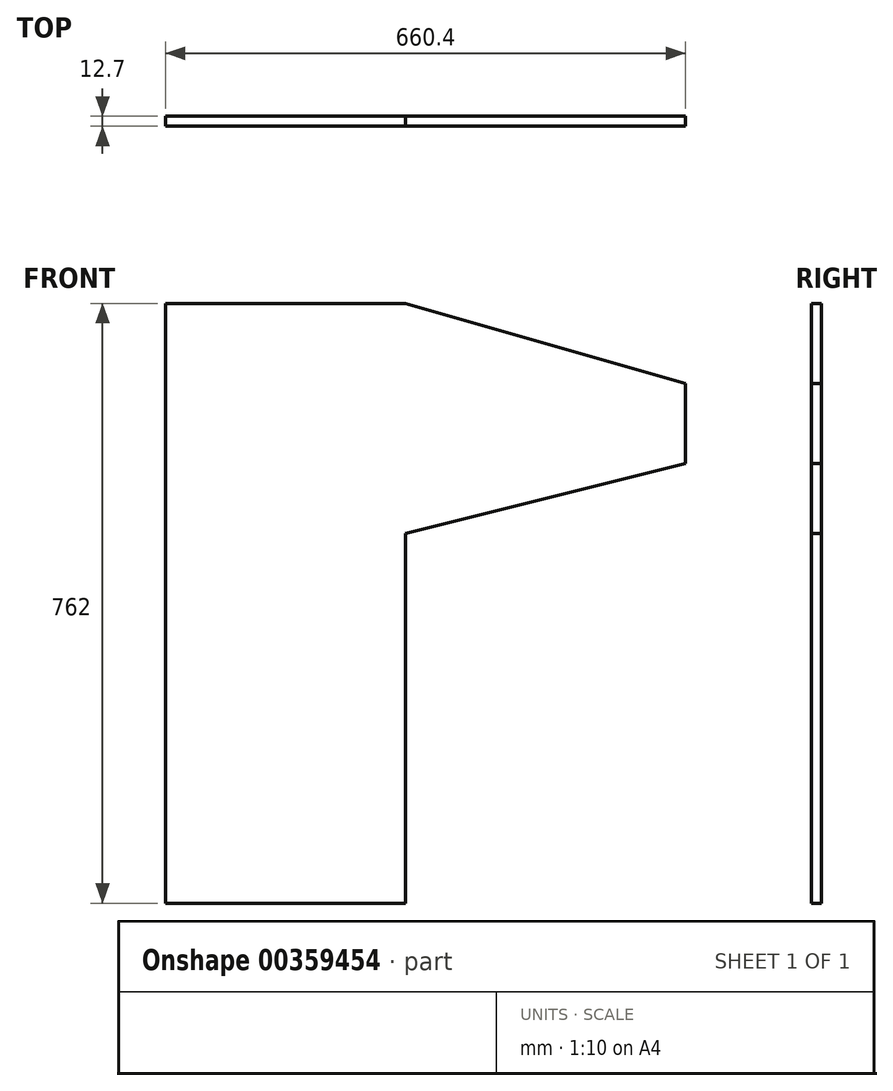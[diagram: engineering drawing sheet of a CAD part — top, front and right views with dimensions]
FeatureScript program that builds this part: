
annotation { "Feature Type Name" : "Feature", "Feature Type Description" : "" }
export const myFeature = defineFeature(function(context is Context, id is Id, definition is map)
    precondition{}
    {
        {
            var Q0;
            Q0=qCreatedBy(makeId("Front.planeOp"),FACE);
            var sketch = newSketch(context, id + "F0", { "sketchPlane" : qUnion([Q0])});
            skLineSegment(sketch, "E0", {"start": v(0, 0) * mm, "end": v(0, 762) * mm});
            skLineSegment(sketch, "E1", {"start": v(0, 762) * mm, "end": v(304.8, 762) * mm});
            skLineSegment(sketch, "E2", {"start": v(304.8, 762) * mm, "end": v(660.4, 660.4) * mm});
            skLineSegment(sketch, "E3", {"start": v(660.4, 660.4) * mm, "end": v(660.4, 558.8) * mm});
            skLineSegment(sketch, "E4", {"start": v(660.4, 558.8) * mm, "end": v(304.8, 469.9) * mm});
            skLineSegment(sketch, "E5", {"start": v(304.8, 469.9) * mm, "end": v(304.8, 0) * mm});
            skLineSegment(sketch, "E6", {"start": v(304.8, 0) * mm, "end": v(0, 0) * mm});
            skSolve(sketch);
        }
        {
            var Q0;
            Q0=makeQuery(id+"F0.imprint","IMPRINT",FACE,{"disambiguationData":[TD([[makeQuery(id+"F0.imprint","IMPRINT",EDGE,{"derivedFrom":sQuery(id+"F0.wireOp",EDGE,"E0")}),-1.0]])]});
            extrude(context, id + "F1", {"entities" : qUnion([Q0]), "oppositeDirection" : true, "depth" : 12.7 * mm});
        }
    });
